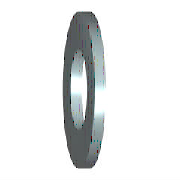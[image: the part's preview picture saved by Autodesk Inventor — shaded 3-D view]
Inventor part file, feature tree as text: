
AUTODESK INVENTOR PART (.ipt)
format: ipt  version: 2020 (Build 240168000, 168)  size: 111,104 bytes
history: native  units: mm (DEFAULTED — no unit token found)
features: other x1, plane x1, sketch x1
ambient origin geometry x7: Origin, YZ Plane, XY Plane, X Axis, Y Axis, Z Axis, Center Point
bodies: Solid1 (feature_tree), Body (feature_tree)
feature tree (3):
  other  "Work Axis1"
  plane  "Work Plane1"
  sketch  "Sketch"  dims[d0=5.3mm d1=10.0mm d2=1.0mm d3=0.0mm d4=0.0mm d5=0.0mm d6=0.0mm d7=0.0mm]
